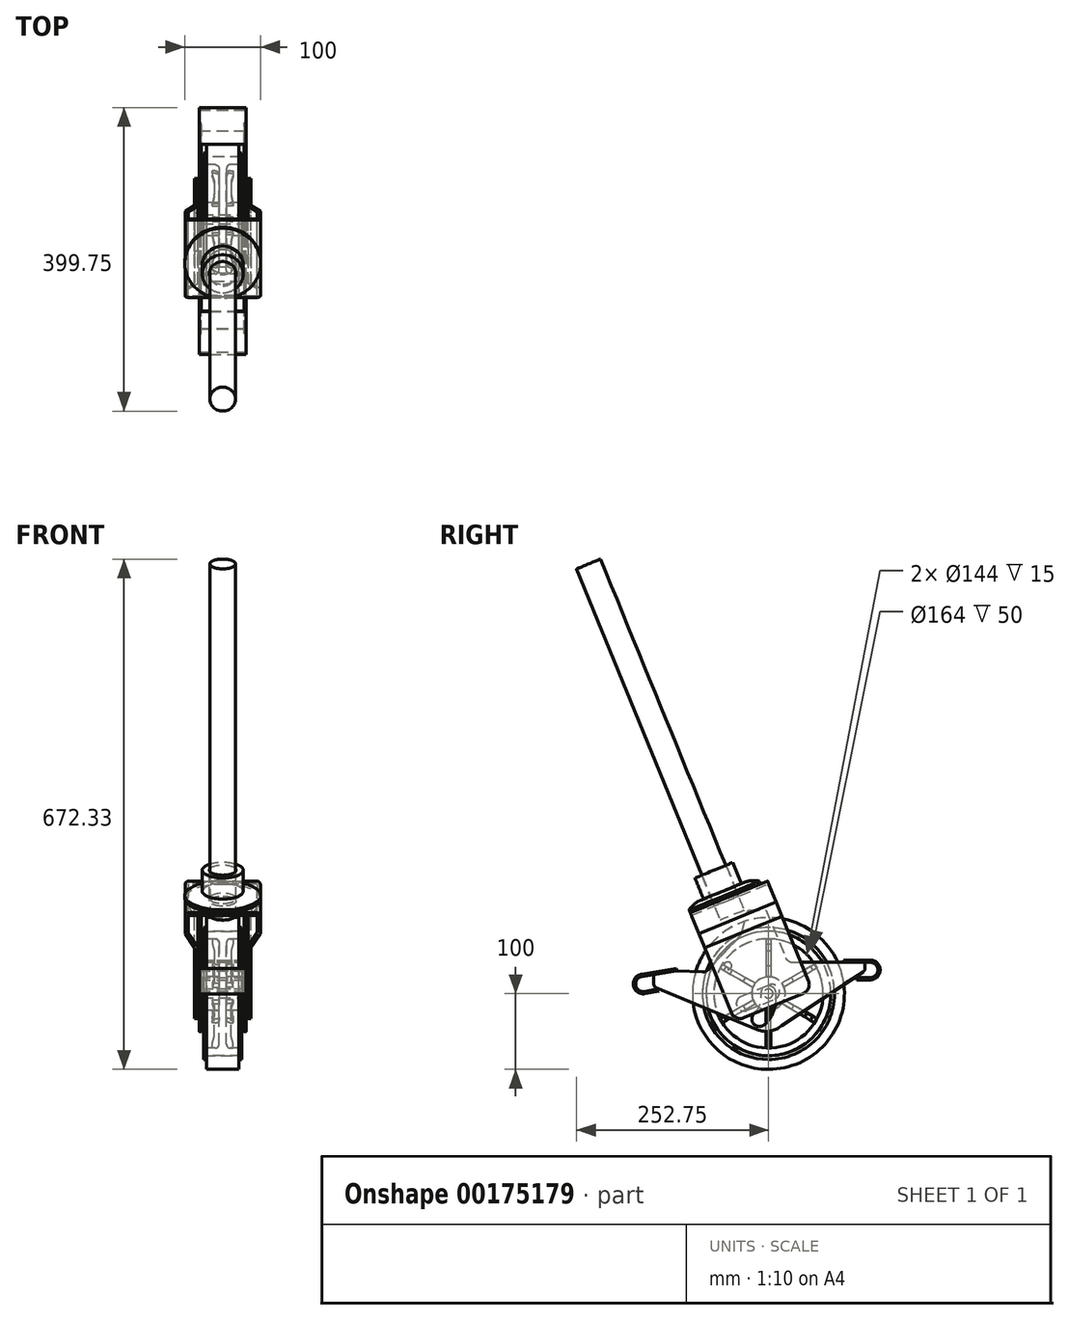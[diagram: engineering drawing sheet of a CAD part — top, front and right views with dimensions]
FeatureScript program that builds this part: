
annotation { "Feature Type Name" : "Feature", "Feature Type Description" : "" }
export const myFeature = defineFeature(function(context is Context, id is Id, definition is map)
    precondition{}
    {
        {
            var Q0;
            Q0=qCreatedBy(makeId("Front.planeOp"),FACE);
            var sketch = newSketch(context, id + "F0", { "sketchPlane" : qUnion([Q0])});
            skLineSegment(sketch, "E0", {"start": v(0, 0) * mm, "end": v(0, 82) * mm});
            skLineSegment(sketch, "E1", {"start": v(0, 82) * mm, "end": v(25, 82) * mm});
            skLineSegment(sketch, "E2", {"start": v(25, 82) * mm, "end": v(25, 72) * mm});
            skLineSegment(sketch, "E3", {"start": v(25, 72) * mm, "end": v(5, 72) * mm});
            skLineSegment(sketch, "E4", {"start": v(5, 72) * mm, "end": v(5, 22) * mm});
            skLineSegment(sketch, "E5", {"start": v(5, 22) * mm, "end": v(27.5, 22) * mm});
            skLineSegment(sketch, "E6", {"start": v(27.5, 22) * mm, "end": v(27.5, 0) * mm});
            skLineSegment(sketch, "E7", {"start": v(27.5, 0) * mm, "end": v(0, 0) * mm});
            skLineSegment(sketch, "E8.MirrorCS", {"start": v(-27.5, 22) * mm, "end": v(-27.5, 0) * mm});
            skLineSegment(sketch, "E9.MirrorCS", {"start": v(0, 82) * mm, "end": v(-25, 82) * mm});
            skLineSegment(sketch, "E10.MirrorCS", {"start": v(-5, 22) * mm, "end": v(-27.5, 22) * mm});
            skLineSegment(sketch, "E11.MirrorCS", {"start": v(-25, 72) * mm, "end": v(-5, 72) * mm});
            skLineSegment(sketch, "E12.MirrorCS", {"start": v(-27.5, 0) * mm, "end": v(0, 0) * mm});
            skLineSegment(sketch, "E13.MirrorCS", {"start": v(-5, 72) * mm, "end": v(-5, 22) * mm});
            skLineSegment(sketch, "E14.MirrorCS", {"start": v(-25, 82) * mm, "end": v(-25, 72) * mm});
            skSolve(sketch);
        }
        {
            var Q0;
            Q0=makeQuery(id+"F0.imprint","IMPRINT",FACE,{"disambiguationData":[TD([[makeQuery(id+"F0.imprint","IMPRINT",EDGE,{"derivedFrom":sQuery(id+"F0.wireOp",EDGE,"E0")}),-1.0]])]});
            var Q1;
            Q1=makeQuery(id+"F0.imprint","IMPRINT",FACE,{"disambiguationData":[TD([[makeQuery(id+"F0.imprint","IMPRINT",EDGE,{"derivedFrom":sQuery(id+"F0.wireOp",EDGE,"E0")}),1.0]])]});
            var Q2;
            Q2=sQuery(id+"F0.wireOp",EDGE,"E12.MirrorCS");
            revolve(context, id + "F1", {"entities" : qUnion([Q0, Q1]), "axis" : qUnion([Q2]), "revolveType" : RevolveType.FULL});
        }
        {
            var Q0;
            Q0=qCreatedBy(makeId("Front.planeOp"),FACE);
            var sketch = newSketch(context, id + "F2", { "sketchPlane" : qUnion([Q0])});
            skLineSegment(sketch, "E15.0.0", {"start": v(5, 67) * mm, "end": v(5, 22) * mm});
            skLineSegment(sketch, "E16", {"start": v(13.5, 22) * mm, "end": v(5, 22) * mm});
            skLineSegment(sketch, "E17", {"start": v(10, 72) * mm, "end": v(13.5, 72) * mm});
            skLineSegment(sketch, "E18", {"start": v(13.5, 72) * mm, "end": v(13.5, 65.54) * mm});
            skLineSegment(sketch, "E19", {"start": v(13.5, 65.54) * mm, "end": v(11, 56.5) * mm});
            skLineSegment(sketch, "E20", {"start": v(11, 56.5) * mm, "end": v(11, 36.5) * mm});
            skLineSegment(sketch, "E21", {"start": v(11, 36.5) * mm, "end": v(13.5, 22) * mm});
            skPoint(sketch, "E22.orphan", {"position": v(5, -72) * mm});
            skPoint(sketch, "E23.visualSharp", {"position": v(5, 72) * mm});
            skArc(sketch, "E23.filletArc", {"start": v(10, 72) * mm, "mid": v(6.46, 70.54) * mm, "end": v(5, 67) * mm});
            skSolve(sketch);
        }
        {
            var Q0;
            Q0=makeQuery(id+"F2.imprint","IMPRINT",FACE,{"disambiguationData":[TD([[makeQuery(id+"F2.imprint","IMPRINT",EDGE,{"derivedFrom":sQuery(id+"F2.wireOp",EDGE,"E15.0.0")}),1.0]])]});
            extrude(context, id + "F3", {"entities" : qUnion([Q0]), "endBound" : BoundingType.SYMMETRIC, "depth" : 6 * mm});
        }
        {
            var Q0;
            Q0=makeQuery(id+"F1.opRevolve","SWEPT_EDGE",EDGE,{"disambiguationData":[OSD([sQuery(id+"F0.wireOp",EDGE,"E3"),sQuery(id+"F0.wireOp",EDGE,"E4")])]});
            var Q1;
            Q1=makeQuery(id+"F1.opRevolve","SWEPT_EDGE",EDGE,{"disambiguationData":[OSD([sQuery(id+"F0.wireOp",EDGE,"E11.MirrorCS"),sQuery(id+"F0.wireOp",EDGE,"E13.MirrorCS")])]});
            fillet(context, id + "F4", {"entities" : qUnion([Q0, Q1]), "radius" : 5 * mm, "tangentPropagation" : true, "allowEdgeOverflow" : false});
        }
        {
            var Q0;
            Q0=makeQuery(id+"F1.opRevolve","SWEPT_FACE",FACE,{"disambiguationData":[OSD([sQuery(id+"F0.wireOp",EDGE,"E6")])]});
            var sketch = newSketch(context, id + "F5", { "sketchPlane" : qUnion([Q0])});
            skCircle(sketch, "E24", {"center": v(0, 0) * mm, "radius": 6 * mm});
            skSolve(sketch);
        }
        {
            var Q0;
            Q0 = qSketchRegion(id + "F5", true);
            extrude(context, id + "F6", {"entities" : qUnion([Q0]), "operationType" : NewBodyOperationType.REMOVE, "endBound" : BoundingType.UP_TO_NEXT, "oppositeDirection" : true, "depth" : 25 * mm});
        }
        {
            var Q0;
            Q0=makeQuery(id+"F3.opExtrude","SWEPT_BODY",BODY,{"disambiguationData":[OSD([sQuery(id+"F2.wireOp",EDGE,"E15.0.0"),sQuery(id+"F2.wireOp",EDGE,"E16"),sQuery(id+"F2.wireOp",EDGE,"E17"),sQuery(id+"F2.wireOp",EDGE,"E18"),sQuery(id+"F2.wireOp",EDGE,"E19"),sQuery(id+"F2.wireOp",EDGE,"E20"),sQuery(id+"F2.wireOp",EDGE,"E21"),sQuery(id+"F2.wireOp",EDGE,"E23.filletArc")])]});
            var Q1;
            Q1=makeQuery(id+"F6.boolean.opBoolean","COPY",FACE,{"derivedFrom":makeQuery(id+"F6.opExtrude","SWEPT_FACE",FACE,{"disambiguationData":[OSD([sQuery(id+"F5.wireOp",EDGE,"E24")])]})});
            circularPattern(context, id + "F7", {"entities" : qUnion([Q0]), "axis" : qUnion([Q1]), "angle" : 360 * degree, "instanceCount" : 6, "equalSpace" : true});
        }
        {
            var Q0;
            Q0=makeQuery(id+"F3.opExtrude","SWEPT_BODY",BODY,{"disambiguationData":[OSD([sQuery(id+"F2.wireOp",EDGE,"E15.0.0"),sQuery(id+"F2.wireOp",EDGE,"E16"),sQuery(id+"F2.wireOp",EDGE,"E17"),sQuery(id+"F2.wireOp",EDGE,"E18"),sQuery(id+"F2.wireOp",EDGE,"E19"),sQuery(id+"F2.wireOp",EDGE,"E20"),sQuery(id+"F2.wireOp",EDGE,"E21"),sQuery(id+"F2.wireOp",EDGE,"E23.filletArc")])]});
            var Q1;
            Q1=makeQuery(id+"F7.opPattern","COPY",BODY,{"derivedFrom":makeQuery(id+"F3.opExtrude","SWEPT_BODY",BODY,{"disambiguationData":[OSD([sQuery(id+"F2.wireOp",EDGE,"E15.0.0"),sQuery(id+"F2.wireOp",EDGE,"E16"),sQuery(id+"F2.wireOp",EDGE,"E17"),sQuery(id+"F2.wireOp",EDGE,"E18"),sQuery(id+"F2.wireOp",EDGE,"E19"),sQuery(id+"F2.wireOp",EDGE,"E20"),sQuery(id+"F2.wireOp",EDGE,"E21"),sQuery(id+"F2.wireOp",EDGE,"E23.filletArc")])]}),"instanceName":"5"});
            var Q2;
            Q2=makeQuery(id+"F7.opPattern","COPY",BODY,{"derivedFrom":makeQuery(id+"F3.opExtrude","SWEPT_BODY",BODY,{"disambiguationData":[OSD([sQuery(id+"F2.wireOp",EDGE,"E15.0.0"),sQuery(id+"F2.wireOp",EDGE,"E16"),sQuery(id+"F2.wireOp",EDGE,"E17"),sQuery(id+"F2.wireOp",EDGE,"E18"),sQuery(id+"F2.wireOp",EDGE,"E19"),sQuery(id+"F2.wireOp",EDGE,"E20"),sQuery(id+"F2.wireOp",EDGE,"E21"),sQuery(id+"F2.wireOp",EDGE,"E23.filletArc")])]}),"instanceName":"4"});
            var Q3;
            Q3=makeQuery(id+"F7.opPattern","COPY",BODY,{"derivedFrom":makeQuery(id+"F3.opExtrude","SWEPT_BODY",BODY,{"disambiguationData":[OSD([sQuery(id+"F2.wireOp",EDGE,"E15.0.0"),sQuery(id+"F2.wireOp",EDGE,"E16"),sQuery(id+"F2.wireOp",EDGE,"E17"),sQuery(id+"F2.wireOp",EDGE,"E18"),sQuery(id+"F2.wireOp",EDGE,"E19"),sQuery(id+"F2.wireOp",EDGE,"E20"),sQuery(id+"F2.wireOp",EDGE,"E21"),sQuery(id+"F2.wireOp",EDGE,"E23.filletArc")])]}),"instanceName":"3"});
            var Q4;
            Q4=makeQuery(id+"F7.opPattern","COPY",BODY,{"derivedFrom":makeQuery(id+"F3.opExtrude","SWEPT_BODY",BODY,{"disambiguationData":[OSD([sQuery(id+"F2.wireOp",EDGE,"E15.0.0"),sQuery(id+"F2.wireOp",EDGE,"E16"),sQuery(id+"F2.wireOp",EDGE,"E17"),sQuery(id+"F2.wireOp",EDGE,"E18"),sQuery(id+"F2.wireOp",EDGE,"E19"),sQuery(id+"F2.wireOp",EDGE,"E20"),sQuery(id+"F2.wireOp",EDGE,"E21"),sQuery(id+"F2.wireOp",EDGE,"E23.filletArc")])]}),"instanceName":"2"});
            var Q5;
            Q5=makeQuery(id+"F7.opPattern","COPY",BODY,{"derivedFrom":makeQuery(id+"F3.opExtrude","SWEPT_BODY",BODY,{"disambiguationData":[OSD([sQuery(id+"F2.wireOp",EDGE,"E15.0.0"),sQuery(id+"F2.wireOp",EDGE,"E16"),sQuery(id+"F2.wireOp",EDGE,"E17"),sQuery(id+"F2.wireOp",EDGE,"E18"),sQuery(id+"F2.wireOp",EDGE,"E19"),sQuery(id+"F2.wireOp",EDGE,"E20"),sQuery(id+"F2.wireOp",EDGE,"E21"),sQuery(id+"F2.wireOp",EDGE,"E23.filletArc")])]}),"instanceName":"1"});
            var Q6;
            Q6=qCreatedBy(makeId("Right.planeOp"),FACE);
            mirror(context, id + "F8", {"entities" : qUnion([Q0, Q1, Q2, Q3, Q4, Q5]), "mirrorPlane" : qUnion([Q6])});
        }
        {
            var Q0;
            Q0=qCreatedBy(makeId("Top.planeOp"),FACE);
            var sketch = newSketch(context, id + "F9", { "sketchPlane" : qUnion([Q0])});
            skLineSegment(sketch, "E25", {"start": v(-890.97, -1000.33) * mm, "end": v(-890.97, -1003.33) * mm});
            skLineSegment(sketch, "E26", {"start": v(-890.97, -1003.33) * mm, "end": v(-894.06, -1003.33) * mm});
            skLineSegment(sketch, "E27", {"start": v(-1283.73, -1003.33) * mm, "end": v(-1283.73, -1396.22) * mm});
            skLineSegment(sketch, "E28", {"start": v(-1283.73, -1396.22) * mm, "end": v(-1690.1, -1396.22) * mm});
            skLineSegment(sketch, "E29", {"start": v(-1690.1, -1396.22) * mm, "end": v(-1690.1, -1802.4) * mm});
            skLineSegment(sketch, "E30", {"start": v(-1690.1, -1802.4) * mm, "end": v(-2098.59, -1802.4) * mm});
            skLineSegment(sketch, "E31", {"start": v(-2098.59, -1802.4) * mm, "end": v(-2098.59, -2210.69) * mm});
            skLineSegment(sketch, "E32", {"start": v(-890.97, -1000.33) * mm, "end": v(-910.8, -1000.33) * mm});
            skLineSegment(sketch, "E33", {"start": v(-910.8, -1000.33) * mm, "end": v(-910.8, -1003.33) * mm});
            skLineSegment(sketch, "E34", {"start": v(-894.06, -1003.33) * mm, "end": v(-894.06, -1005.54) * mm});
            skLineSegment(sketch, "E35", {"start": v(-894.06, -1005.54) * mm, "end": v(-907.53, -1005.54) * mm});
            skLineSegment(sketch, "E36", {"start": v(-907.53, -1005.54) * mm, "end": v(-907.53, -1003.33) * mm});
            skLineSegment(sketch, "E37.trimOffspring", {"start": v(-907.53, -1003.33) * mm, "end": v(-910.8, -1003.33) * mm});
            skLineSegment(sketch, "E38", {"start": v(25, -87) * mm, "end": v(21.48, -87) * mm});
            skLineSegment(sketch, "E39", {"start": v(21.48, -87) * mm, "end": v(21.48, -100) * mm});
            skLineSegment(sketch, "E40", {"start": v(21.48, -100) * mm, "end": v(-21.52, -100) * mm});
            skLineSegment(sketch, "E41", {"start": v(-21.52, -100) * mm, "end": v(-21.52, -87) * mm});
            skLineSegment(sketch, "E42", {"start": v(-21.52, -87) * mm, "end": v(-25.02, -87) * mm});
            skLineSegment(sketch, "E43.0", {"start": v(25, -87) * mm, "end": v(25, -82) * mm});
            skLineSegment(sketch, "E43.1", {"start": v(-25, -87) * mm, "end": v(-25, -82) * mm});
            skLineSegment(sketch, "E44", {"start": v(-25, -82) * mm, "end": v(25, -82) * mm});
            skPoint(sketch, "E45.orphan", {"position": v(25, 82) * mm});
            skPoint(sketch, "E46.orphan", {"position": v(-25, 82) * mm});
            skSolve(sketch);
        }
        {
            var Q0;
            {var subQ3=sQuery(id+"F9.wireOp",EDGE,"E39");Q0=makeQuery(id+"F9.imprint","IMPRINT",FACE,{"disambiguationData":[TD([[makeQuery(id+"F9.imprint","IMPRINT",EDGE,{"derivedFrom":subQ3}),-1.0]])]});}
            var Q1;
            Q1=makeQuery(id+"F1.opRevolve","SWEPT_FACE",FACE,{"disambiguationData":[OSD([sQuery(id+"F0.wireOp",EDGE,"E5")])]});
            revolve(context, id + "F10", {"entities" : qUnion([Q0]), "axis" : qUnion([Q1]), "revolveType" : RevolveType.FULL});
        }
        {
            var Q0;
            Q0=qCreatedBy(makeId("Right.planeOp"),FACE);
            cPlane(context, id + "F11", {"entities" : qUnion([Q0]), "cplaneType" : CPlaneType.OFFSET, "offset" : 28 * mm, "width" : 150 * mm, "height" : 150 * mm});
        }
        {
            var Q0;
            Q0=qCreatedBy(id+"F11.planeOp",FACE);
            var sketch = newSketch(context, id + "F12", { "sketchPlane" : qUnion([Q0])});
            skArc(sketch, "E47", {"start": v(9.92, 1.23) * mm, "mid": v(-1.23, 9.92) * mm, "end": v(-9.92, -1.23) * mm});
            skLineSegment(sketch, "E48", {"start": v(31.86, 41) * mm, "end": v(127, 41) * mm});
            skLineSegment(sketch, "E49", {"start": v(127, 41) * mm, "end": v(127, 32.7) * mm});
            skArc(sketch, "E50", {"start": v(-14.51, -47.7) * mm, "mid": v(1.93, -49.6) * mm, "end": v(16.88, -42.47) * mm});
            skLineSegment(sketch, "E51", {"start": v(124.75, 28.52) * mm, "end": v(16.88, -42.47) * mm});
            skLineSegment(sketch, "E52", {"start": v(-150.97, 25) * mm, "end": v(-150.97, 12.34) * mm});
            skLineSegment(sketch, "E53", {"start": v(-147.89, 7.72) * mm, "end": v(-14.51, -47.7) * mm});
            skLineSegment(sketch, "E54", {"start": v(-150.97, 25) * mm, "end": v(-120.97, 30) * mm});
            skLineSegment(sketch, "E55", {"start": v(-120.97, 30) * mm, "end": v(-87.39, 28.24) * mm});
            skLineSegment(sketch, "E56", {"start": v(-79.6, 31.36) * mm, "end": v(-37.27, 76.13) * mm});
            skLineSegment(sketch, "E57", {"start": v(-34.88, 80.41) * mm, "end": v(-27, 109.83) * mm});
            skLineSegment(sketch, "E58", {"start": v(-27, 109.83) * mm, "end": v(-3, 109.83) * mm});
            skLineSegment(sketch, "E59", {"start": v(-3, 109.83) * mm, "end": v(22.6, 47.22) * mm});
            skPoint(sketch, "E60.visualSharp", {"position": v(-150.97, 9) * mm});
            skArc(sketch, "E60.filletArc", {"start": v(-150.97, 12.34) * mm, "mid": v(-150.13, 9.56) * mm, "end": v(-147.89, 7.72) * mm});
            skPoint(sketch, "E61.visualSharp", {"position": v(127, 30) * mm});
            skArc(sketch, "E61.filletArc", {"start": v(124.75, 28.52) * mm, "mid": v(126.4, 30.32) * mm, "end": v(127, 32.7) * mm});
            skPoint(sketch, "E62.visualSharp", {"position": v(25.14, 41) * mm});
            skArc(sketch, "E62.filletArc", {"start": v(22.6, 47.22) * mm, "mid": v(26.28, 42.7) * mm, "end": v(31.86, 41) * mm});
            skPoint(sketch, "E63.visualSharp", {"position": v(-82.77, 28) * mm});
            skArc(sketch, "E63.filletArc", {"start": v(-87.39, 28.24) * mm, "mid": v(-83.15, 28.94) * mm, "end": v(-79.6, 31.36) * mm});
            skPoint(sketch, "E64.visualSharp", {"position": v(-35.54, 77.97) * mm});
            skArc(sketch, "E64.filletArc", {"start": v(-37.27, 76.13) * mm, "mid": v(-35.81, 78.13) * mm, "end": v(-34.88, 80.41) * mm});
            skArc(sketch, "E65", {"start": v(-18.77, -26.43) * mm, "mid": v(-18.97, -40.57) * mm, "end": v(-4.83, -40.77) * mm});
            skArc(sketch, "E66", {"start": v(-4.83, -40.77) * mm, "mid": v(7.48, -21.5) * mm, "end": v(9.92, 1.23) * mm});
            skArc(sketch, "E67.0", {"start": v(-18.77, -26.43) * mm, "mid": v(-11.39, -14.87) * mm, "end": v(-9.92, -1.23) * mm});
            skCircle(sketch, "E68", {"center": v(-53.5, 36.5) * mm, "radius": 5 * mm});
            skSolve(sketch);
        }
        {
            var Q0;
            Q0 = qSketchRegion(id + "F12", true);
            extrude(context, id + "F13", {"entities" : qUnion([Q0]), "depth" : 3 * mm});
        }
        {
            var Q0;
            Q0=makeQuery(id+"F13.opExtrude","SWEPT_BODY",BODY,{"disambiguationData":[OSD([sQuery(id+"F12.wireOp",EDGE,"E47"),sQuery(id+"F12.wireOp",EDGE,"E48"),sQuery(id+"F12.wireOp",EDGE,"E49"),sQuery(id+"F12.wireOp",EDGE,"E50"),sQuery(id+"F12.wireOp",EDGE,"E51"),sQuery(id+"F12.wireOp",EDGE,"E52"),sQuery(id+"F12.wireOp",EDGE,"E53"),sQuery(id+"F12.wireOp",EDGE,"E54"),sQuery(id+"F12.wireOp",EDGE,"E55"),sQuery(id+"F12.wireOp",EDGE,"E56"),sQuery(id+"F12.wireOp",EDGE,"E57"),sQuery(id+"F12.wireOp",EDGE,"E58"),sQuery(id+"F12.wireOp",EDGE,"E59"),sQuery(id+"F12.wireOp",EDGE,"E60.filletArc"),sQuery(id+"F12.wireOp",EDGE,"E61.filletArc"),sQuery(id+"F12.wireOp",EDGE,"E62.filletArc"),sQuery(id+"F12.wireOp",EDGE,"E63.filletArc"),sQuery(id+"F12.wireOp",EDGE,"E64.filletArc"),sQuery(id+"F12.wireOp",EDGE,"E65"),sQuery(id+"F12.wireOp",EDGE,"E66"),sQuery(id+"F12.wireOp",EDGE,"E67.0"),sQuery(id+"F12.wireOp",EDGE,"E68")])]});
            var Q1;
            Q1=qCreatedBy(makeId("Right.planeOp"),FACE);
            mirror(context, id + "F14", {"entities" : qUnion([Q0]), "mirrorPlane" : qUnion([Q1])});
        }
        {
            var Q0;
            Q0=makeQuery(id+"F13.opExtrude","CAP_FACE",FACE,{"disambiguationData":[OSD([sQuery(id+"F12.wireOp",EDGE,"E47"),sQuery(id+"F12.wireOp",EDGE,"E48"),sQuery(id+"F12.wireOp",EDGE,"E49"),sQuery(id+"F12.wireOp",EDGE,"E50"),sQuery(id+"F12.wireOp",EDGE,"E51"),sQuery(id+"F12.wireOp",EDGE,"E52"),sQuery(id+"F12.wireOp",EDGE,"E53"),sQuery(id+"F12.wireOp",EDGE,"E54"),sQuery(id+"F12.wireOp",EDGE,"E55"),sQuery(id+"F12.wireOp",EDGE,"E56"),sQuery(id+"F12.wireOp",EDGE,"E57"),sQuery(id+"F12.wireOp",EDGE,"E58"),sQuery(id+"F12.wireOp",EDGE,"E59"),sQuery(id+"F12.wireOp",EDGE,"E60.filletArc"),sQuery(id+"F12.wireOp",EDGE,"E61.filletArc"),sQuery(id+"F12.wireOp",EDGE,"E62.filletArc"),sQuery(id+"F12.wireOp",EDGE,"E63.filletArc"),sQuery(id+"F12.wireOp",EDGE,"E64.filletArc"),sQuery(id+"F12.wireOp",EDGE,"E65"),sQuery(id+"F12.wireOp",EDGE,"E66"),sQuery(id+"F12.wireOp",EDGE,"E67.0"),sQuery(id+"F12.wireOp",EDGE,"E68")])],"isStart":false});
            var sketch = newSketch(context, id + "F15", { "sketchPlane" : qUnion([Q0])});
            skLineSegment(sketch, "E69.1", {"start": v(-166.61, 22.4) * mm, "end": v(-120.97, 30) * mm});
            skArc(sketch, "E70", {"start": v(-166.61, 22.4) * mm, "mid": v(-174.8, 10.74) * mm, "end": v(-163.03, 2.72) * mm});
            skPoint(sketch, "E71.orphan", {"position": v(-150.97, 25) * mm});
            skLineSegment(sketch, "E72", {"start": v(-163.03, 2.72) * mm, "end": v(-144.61, 6.36) * mm});
            skLineSegment(sketch, "E73.0", {"start": v(-167.1, 25.35) * mm, "end": v(-121.46, 32.96) * mm});
            skArc(sketch, "E73.1", {"start": v(-167.1, 25.35) * mm, "mid": v(-177.76, 10.2) * mm, "end": v(-162.45, -0.22) * mm});
            skLineSegment(sketch, "E73.2", {"start": v(-162.45, -0.22) * mm, "end": v(-144.03, 3.42) * mm});
            skLineSegment(sketch, "E74", {"start": v(-120.97, 30) * mm, "end": v(-121.46, 32.96) * mm});
            skLineSegment(sketch, "E75", {"start": v(-144.03, 3.42) * mm, "end": v(-144.61, 6.36) * mm});
            skSolve(sketch);
        }
        {
            var Q0;
            Q0 = qSketchRegion(id + "F15", true);
            var Q1;
            Q1=makeQuery(id+"F14.opPattern","COPY",FACE,{"derivedFrom":makeQuery(id+"F13.opExtrude","CAP_FACE",FACE,{"disambiguationData":[OSD([sQuery(id+"F12.wireOp",EDGE,"E47"),sQuery(id+"F12.wireOp",EDGE,"E48"),sQuery(id+"F12.wireOp",EDGE,"E49"),sQuery(id+"F12.wireOp",EDGE,"E50"),sQuery(id+"F12.wireOp",EDGE,"E51"),sQuery(id+"F12.wireOp",EDGE,"E52"),sQuery(id+"F12.wireOp",EDGE,"E53"),sQuery(id+"F12.wireOp",EDGE,"E54"),sQuery(id+"F12.wireOp",EDGE,"E55"),sQuery(id+"F12.wireOp",EDGE,"E56"),sQuery(id+"F12.wireOp",EDGE,"E57"),sQuery(id+"F12.wireOp",EDGE,"E58"),sQuery(id+"F12.wireOp",EDGE,"E59"),sQuery(id+"F12.wireOp",EDGE,"E60.filletArc"),sQuery(id+"F12.wireOp",EDGE,"E61.filletArc"),sQuery(id+"F12.wireOp",EDGE,"E62.filletArc"),sQuery(id+"F12.wireOp",EDGE,"E63.filletArc"),sQuery(id+"F12.wireOp",EDGE,"E64.filletArc"),sQuery(id+"F12.wireOp",EDGE,"E65"),sQuery(id+"F12.wireOp",EDGE,"E66"),sQuery(id+"F12.wireOp",EDGE,"E67.0"),sQuery(id+"F12.wireOp",EDGE,"E68")])],"isStart":false}),"instanceName":"1"});
            extrude(context, id + "F16", {"entities" : qUnion([Q0]), "endBound" : BoundingType.UP_TO_SURFACE, "oppositeDirection" : true, "endBoundEntityFace" : qUnion([Q1]), "depth" : 25 * mm});
        }
        {
            var Q0;
            Q0=makeQuery(id+"F13.opExtrude","CAP_FACE",FACE,{"disambiguationData":[OSD([sQuery(id+"F12.wireOp",EDGE,"E47"),sQuery(id+"F12.wireOp",EDGE,"E48"),sQuery(id+"F12.wireOp",EDGE,"E49"),sQuery(id+"F12.wireOp",EDGE,"E50"),sQuery(id+"F12.wireOp",EDGE,"E51"),sQuery(id+"F12.wireOp",EDGE,"E52"),sQuery(id+"F12.wireOp",EDGE,"E53"),sQuery(id+"F12.wireOp",EDGE,"E54"),sQuery(id+"F12.wireOp",EDGE,"E55"),sQuery(id+"F12.wireOp",EDGE,"E56"),sQuery(id+"F12.wireOp",EDGE,"E57"),sQuery(id+"F12.wireOp",EDGE,"E58"),sQuery(id+"F12.wireOp",EDGE,"E59"),sQuery(id+"F12.wireOp",EDGE,"E60.filletArc"),sQuery(id+"F12.wireOp",EDGE,"E61.filletArc"),sQuery(id+"F12.wireOp",EDGE,"E62.filletArc"),sQuery(id+"F12.wireOp",EDGE,"E63.filletArc"),sQuery(id+"F12.wireOp",EDGE,"E64.filletArc"),sQuery(id+"F12.wireOp",EDGE,"E65"),sQuery(id+"F12.wireOp",EDGE,"E66"),sQuery(id+"F12.wireOp",EDGE,"E67.0"),sQuery(id+"F12.wireOp",EDGE,"E68")])],"isStart":false});
            var sketch = newSketch(context, id + "F17", { "sketchPlane" : qUnion([Q0])});
            skLineSegment(sketch, "E76.0.0", {"start": v(-37.27, 76.13) * mm, "end": v(-79.6, 31.36) * mm});
            skArc(sketch, "E76.0.1", {"start": v(-79.6, 31.36) * mm, "mid": v(-83.15, 28.94) * mm, "end": v(-87.39, 28.24) * mm});
            skLineSegment(sketch, "E76.0.2", {"start": v(-87.39, 28.24) * mm, "end": v(-120.97, 30) * mm});
            skLineSegment(sketch, "E76.0.3", {"start": v(-120.97, 30) * mm, "end": v(-150.97, 25) * mm});
            skLineSegment(sketch, "E76.0.4", {"start": v(-150.97, 25) * mm, "end": v(-150.97, 12.34) * mm});
            skArc(sketch, "E76.0.5", {"start": v(-150.97, 12.34) * mm, "mid": v(-150.13, 9.56) * mm, "end": v(-147.89, 7.72) * mm});
            skLineSegment(sketch, "E76.0.6", {"start": v(-147.89, 7.72) * mm, "end": v(-14.51, -47.7) * mm});
            skArc(sketch, "E76.0.7", {"start": v(-14.51, -47.7) * mm, "mid": v(1.93, -49.6) * mm, "end": v(16.88, -42.47) * mm});
            skLineSegment(sketch, "E76.0.11", {"start": v(127, 41) * mm, "end": v(99, 41) * mm});
            skArc(sketch, "E76.0.12", {"start": v(31.86, 41) * mm, "mid": v(26.28, 42.7) * mm, "end": v(22.6, 47.22) * mm});
            skLineSegment(sketch, "E76.0.13", {"start": v(22.6, 47.22) * mm, "end": v(-3, 109.83) * mm});
            skLineSegment(sketch, "E76.0.14", {"start": v(-3, 109.83) * mm, "end": v(-27, 109.83) * mm});
            skLineSegment(sketch, "E76.0.15", {"start": v(-27, 109.83) * mm, "end": v(-34.88, 80.41) * mm});
            skArc(sketch, "E76.0.16", {"start": v(-34.88, 80.41) * mm, "mid": v(-35.81, 78.13) * mm, "end": v(-37.27, 76.13) * mm});
            skLineSegment(sketch, "E76.1", {"start": v(99, 41) * mm, "end": v(134, 41) * mm});
            skArc(sketch, "E77", {"start": v(133.94, 21) * mm, "mid": v(144, 30.97) * mm, "end": v(134, 41) * mm});
            skLineSegment(sketch, "E78", {"start": v(133.94, 21) * mm, "end": v(116.29, 21) * mm});
            skLineSegment(sketch, "E79.0", {"start": v(133.94, 18) * mm, "end": v(116.29, 18) * mm});
            skArc(sketch, "E80.0", {"start": v(133.92, 18) * mm, "mid": v(147, 30.96) * mm, "end": v(134, 44) * mm});
            skLineSegment(sketch, "E81.0", {"start": v(99, 44) * mm, "end": v(134, 44) * mm});
            skLineSegment(sketch, "E82", {"start": v(99, 41) * mm, "end": v(99, 44) * mm});
            skLineSegment(sketch, "E83", {"start": v(116.29, 21) * mm, "end": v(116.29, 18) * mm});
            skSolve(sketch);
        }
        {
            var Q0;
            Q0 = qSketchRegion(id + "F17", true);
            var Q1;
            Q1=makeQuery(id+"F14.opPattern","COPY",FACE,{"derivedFrom":makeQuery(id+"F13.opExtrude","CAP_FACE",FACE,{"disambiguationData":[OSD([sQuery(id+"F12.wireOp",EDGE,"E47"),sQuery(id+"F12.wireOp",EDGE,"E48"),sQuery(id+"F12.wireOp",EDGE,"E49"),sQuery(id+"F12.wireOp",EDGE,"E50"),sQuery(id+"F12.wireOp",EDGE,"E51"),sQuery(id+"F12.wireOp",EDGE,"E52"),sQuery(id+"F12.wireOp",EDGE,"E53"),sQuery(id+"F12.wireOp",EDGE,"E54"),sQuery(id+"F12.wireOp",EDGE,"E55"),sQuery(id+"F12.wireOp",EDGE,"E56"),sQuery(id+"F12.wireOp",EDGE,"E57"),sQuery(id+"F12.wireOp",EDGE,"E58"),sQuery(id+"F12.wireOp",EDGE,"E59"),sQuery(id+"F12.wireOp",EDGE,"E60.filletArc"),sQuery(id+"F12.wireOp",EDGE,"E61.filletArc"),sQuery(id+"F12.wireOp",EDGE,"E62.filletArc"),sQuery(id+"F12.wireOp",EDGE,"E63.filletArc"),sQuery(id+"F12.wireOp",EDGE,"E64.filletArc"),sQuery(id+"F12.wireOp",EDGE,"E65"),sQuery(id+"F12.wireOp",EDGE,"E66"),sQuery(id+"F12.wireOp",EDGE,"E67.0"),sQuery(id+"F12.wireOp",EDGE,"E68")])],"isStart":false}),"instanceName":"1"});
            extrude(context, id + "F18", {"entities" : qUnion([Q0]), "endBound" : BoundingType.UP_TO_SURFACE, "oppositeDirection" : true, "endBoundEntityFace" : qUnion([Q1]), "depth" : 25 * mm});
        }
        {
            var Q0;
            Q0=makeQuery(id+"F13.opExtrude","SWEPT_FACE",FACE,{"disambiguationData":[OSD([sQuery(id+"F12.wireOp",EDGE,"E59")])]});
            cPlane(context, id + "F19", {"entities" : qUnion([Q0]), "cplaneType" : CPlaneType.OFFSET, "offset" : 38.8 * mm, "oppositeDirection" : true, "width" : 150 * mm, "height" : 150 * mm});
        }
        {
            var Q0;
            Q0=qCreatedBy(id+"F19.planeOp",FACE);
            var sketch = newSketch(context, id + "F20", { "sketchPlane" : qUnion([Q0])});
            skLineSegment(sketch, "E84.top", {"start": v(44.5, 133.5) * mm, "end": v(0, 133.5) * mm});
            skLineSegment(sketch, "E84.left", {"start": v(33, -17.5) * mm, "end": v(33, 88.65) * mm});
            skLineSegment(sketch, "E85", {"start": v(45.5, 132.5) * mm, "end": v(45.5, 108.65) * mm});
            skLineSegment(sketch, "E86", {"start": v(45.5, 108.65) * mm, "end": v(33, 88.65) * mm});
            skLineSegment(sketch, "E87", {"start": v(0, 98.73) * mm, "end": v(0, 133.5) * mm, "construction": true});
            skLineSegment(sketch, "E88.0", {"start": v(44.5, 137.5) * mm, "end": v(0, 137.5) * mm});
            skLineSegment(sketch, "E88.1", {"start": v(49.5, 132.5) * mm, "end": v(49.5, 107.5) * mm});
            skLineSegment(sketch, "E88.2", {"start": v(49.5, 107.5) * mm, "end": v(37, 87.5) * mm});
            skLineSegment(sketch, "E88.3", {"start": v(37, -17.5) * mm, "end": v(37, 87.5) * mm});
            skLineSegment(sketch, "E89", {"start": v(37, -17.5) * mm, "end": v(33, -17.5) * mm});
            skLineSegment(sketch, "E90.MirrorCS", {"start": v(-37, -17.5) * mm, "end": v(-33, -17.5) * mm});
            skLineSegment(sketch, "E91.MirrorCS", {"start": v(-44.5, 137.5) * mm, "end": v(0, 137.5) * mm});
            skLineSegment(sketch, "E92.MirrorCS", {"start": v(-45.5, 108.65) * mm, "end": v(-33, 88.65) * mm});
            skLineSegment(sketch, "E93.MirrorCS", {"start": v(-45.5, 132.5) * mm, "end": v(-45.5, 108.65) * mm});
            skLineSegment(sketch, "E94.MirrorCS", {"start": v(-33, -17.5) * mm, "end": v(-33, 88.65) * mm});
            skLineSegment(sketch, "E95.MirrorCS", {"start": v(-49.5, 132.5) * mm, "end": v(-49.5, 107.5) * mm});
            skLineSegment(sketch, "E96.MirrorCS", {"start": v(-37, -17.5) * mm, "end": v(-37, 87.5) * mm});
            skLineSegment(sketch, "E97.MirrorCS", {"start": v(-44.5, 133.5) * mm, "end": v(0, 133.5) * mm});
            skLineSegment(sketch, "E98.MirrorCS", {"start": v(-49.5, 107.5) * mm, "end": v(-37, 87.5) * mm});
            skPoint(sketch, "E99.visualSharp", {"position": v(45.5, 133.5) * mm});
            skArc(sketch, "E99.filletArc", {"start": v(45.5, 132.5) * mm, "mid": v(45.2, 133.2) * mm, "end": v(44.5, 133.5) * mm});
            skPoint(sketch, "E100.visualSharp", {"position": v(-45.5, 133.5) * mm});
            skArc(sketch, "E100.filletArc", {"start": v(-44.5, 133.5) * mm, "mid": v(-45.2, 133.2) * mm, "end": v(-45.5, 132.5) * mm});
            skPoint(sketch, "E101.visualSharp", {"position": v(-49.5, 137.5) * mm});
            skArc(sketch, "E101.filletArc", {"start": v(-44.5, 137.5) * mm, "mid": v(-48.04, 136.04) * mm, "end": v(-49.5, 132.5) * mm});
            skPoint(sketch, "E102.visualSharp", {"position": v(49.5, 137.5) * mm});
            skArc(sketch, "E102.filletArc", {"start": v(49.5, 132.5) * mm, "mid": v(48.04, 136.04) * mm, "end": v(44.5, 137.5) * mm});
            skSolve(sketch);
        }
        {
            var Q0;
            Q0 = qSketchRegion(id + "F20", true);
            extrude(context, id + "F21", {"entities" : qUnion([Q0]), "endBound" : BoundingType.SYMMETRIC, "oppositeDirection" : true, "depth" : 110 * mm});
        }
        {
            var Q0;
            Q0=makeQuery(id+"F21.opExtrude","CAP_EDGE",EDGE,{"disambiguationData":[OSD([sQuery(id+"F20.wireOp",EDGE,"E90.MirrorCS")])],"isStart":true});
            var Q1;
            Q1=makeQuery(id+"F21.opExtrude","CAP_EDGE",EDGE,{"disambiguationData":[OSD([sQuery(id+"F20.wireOp",EDGE,"E90.MirrorCS")])],"isStart":false});
            var Q2;
            Q2=makeQuery(id+"F21.opExtrude","CAP_EDGE",EDGE,{"disambiguationData":[OSD([sQuery(id+"F20.wireOp",EDGE,"E89")])],"isStart":false});
            var Q3;
            Q3=makeQuery(id+"F21.opExtrude","CAP_EDGE",EDGE,{"disambiguationData":[OSD([sQuery(id+"F20.wireOp",EDGE,"E89")])],"isStart":true});
            fillet(context, id + "F22", {"entities" : qUnion([Q0, Q1, Q2, Q3]), "radius" : 13 * mm, "tangentPropagation" : true, "allowEdgeOverflow" : false});
        }
        {
            var Q0;
            Q0=makeQuery(id+"F21.opExtrude","SWEPT_FACE",FACE,{"disambiguationData":[OSD([sQuery(id+"F20.wireOp",EDGE,"E88.3")])]});
            var sketch = newSketch(context, id + "F23", { "sketchPlane" : qUnion([Q0])});
            skLineSegment(sketch, "E103", {"start": v(36.85, -15.07) * mm, "end": v(-17.88, 7.3) * mm, "construction": true});
            skArc(sketch, "E104", {"start": v(-0.8, 11.13) * mm, "mid": v(-13.92, 5.59) * mm, "end": v(-8.18, -7.45) * mm});
            skArc(sketch, "E105", {"start": v(28.61, -22.5) * mm, "mid": v(41.65, -17.03) * mm, "end": v(36.18, -4) * mm});
            skLineSegment(sketch, "E106", {"start": v(-8.18, -7.45) * mm, "end": v(28.61, -22.5) * mm});
            skLineSegment(sketch, "E107", {"start": v(-0.9, 11.17) * mm, "end": v(36.18, -4) * mm});
            skSolve(sketch);
        }
        {
            var Q0;
            Q0 = qSketchRegion(id + "F23", true);
            extrude(context, id + "F24", {"entities" : qUnion([Q0]), "operationType" : NewBodyOperationType.REMOVE, "endBound" : BoundingType.UP_TO_NEXT, "oppositeDirection" : true, "depth" : 25 * mm});
        }
        {
            var Q0;
            Q0=makeQuery(id+"F1.opRevolve","SWEPT_FACE",FACE,{"disambiguationData":[OSD([sQuery(id+"F0.wireOp",EDGE,"E14.MirrorCS")])]});
            cPlane(context, id + "F25", {"entities" : qUnion([Q0]), "cplaneType" : CPlaneType.OFFSET, "offset" : 25 * mm, "oppositeDirection" : true, "width" : 150 * mm, "height" : 150 * mm});
        }
        {
            var Q0;
            Q0=makeQuery(id+"F21.opExtrude","SWEPT_FACE",FACE,{"disambiguationData":[OSD([sQuery(id+"F20.wireOp",EDGE,"E88.0"),sQuery(id+"F20.wireOp",EDGE,"E91.MirrorCS")])]});
            var sketch = newSketch(context, id + "F26", { "sketchPlane" : qUnion([Q0])});
            skCircle(sketch, "E108", {"center": v(0, -5) * mm, "radius": 17.5 * mm});
            skPoint(sketch, "E108.centerSnap0", {"position": v(0, -55) * mm});
            skSolve(sketch);
        }
        {
            var Q0;
            Q0 = qSketchRegion(id + "F26", true);
            extrude(context, id + "F27", {"entities" : qUnion([Q0]), "operationType" : NewBodyOperationType.REMOVE, "endBound" : BoundingType.UP_TO_NEXT, "oppositeDirection" : true, "depth" : 25 * mm});
        }
        {
            var Q0;
            Q0=qCreatedBy(id+"F25.planeOp",FACE);
            var sketch = newSketch(context, id + "F28", { "sketchPlane" : qUnion([Q0])});
            skLineSegment(sketch, "E109", {"start": v(56.68, 125.38) * mm, "end": v(60.46, 134.63) * mm});
            skLineSegment(sketch, "E110", {"start": v(102.96, 106.45) * mm, "end": v(104.47, 110.15) * mm});
            skLineSegment(sketch, "E111", {"start": v(89.08, 122.93) * mm, "end": v(60.46, 134.63) * mm});
            skArc(sketch, "E112", {"start": v(89.08, 122.93) * mm, "mid": v(97.76, 117.72) * mm, "end": v(104.47, 110.15) * mm});
            skLineSegment(sketch, "E113.0", {"start": v(102.96, 106.45) * mm, "end": v(56.68, 125.38) * mm});
            skPoint(sketch, "E114.orphan", {"position": v(1.14, 148.08) * mm});
            skSolve(sketch);
        }
        {
            var Q0;
            Q0 = qSketchRegion(id + "F28", true);
            var Q1;
            Q1=sQuery(id+"F28.wireOp",EDGE,"E109");
            revolve(context, id + "F29", {"entities" : qUnion([Q0]), "axis" : qUnion([Q1]), "revolveType" : RevolveType.FULL});
        }
        {
            var Q0;
            Q0=makeQuery(id+"F29.opRevolve","SWEPT_FACE",FACE,{"disambiguationData":[OSD([sQuery(id+"F28.wireOp",EDGE,"E111")])]});
            var sketch = newSketch(context, id + "F30", { "sketchPlane" : qUnion([Q0])});
            skCircle(sketch, "E115", {"center": v(0, -5) * mm, "radius": 17.5 * mm});
            skSolve(sketch);
        }
        {
            var Q0;
            Q0 = qSketchRegion(id + "F30", true);
            extrude(context, id + "F31", {"entities" : qUnion([Q0]), "operationType" : NewBodyOperationType.REMOVE, "oppositeDirection" : true, "depth" : 10 * mm});
        }
        {
            var Q0;
            Q0=makeQuery(id+"F29.opRevolve","SWEPT_FACE",FACE,{"disambiguationData":[OSD([sQuery(id+"F28.wireOp",EDGE,"E111")])]});
            var sketch = newSketch(context, id + "F32", { "sketchPlane" : qUnion([Q0])});
            skCircle(sketch, "E116", {"center": v(0, -5) * mm, "radius": 27 * mm});
            skCircle(sketch, "E117.0", {"center": v(0, -5) * mm, "radius": 17.5 * mm});
            skSolve(sketch);
        }
        {
            var Q0;
            Q0 = qSketchRegion(id + "F32", true);
            extrude(context, id + "F33", {"entities" : qUnion([Q0]), "operationType" : NewBodyOperationType.ADD, "depth" : 30 * mm});
        }
        {
            var Q0;
            Q0=makeQuery(id+"F21.opExtrude","SWEPT_FACE",FACE,{"disambiguationData":[OSD([sQuery(id+"F20.wireOp",EDGE,"E84.top"),sQuery(id+"F20.wireOp",EDGE,"E97.MirrorCS")])]});
            cPlane(context, id + "F34", {"entities" : qUnion([Q0]), "cplaneType" : CPlaneType.OFFSET, "offset" : 20 * mm, "width" : 150 * mm, "height" : 150 * mm});
        }
        {
            var Q0;
            Q0=qCreatedBy(id+"F34.planeOp",FACE);
            var sketch = newSketch(context, id + "F35", { "sketchPlane" : qUnion([Q0])});
            skCircle(sketch, "E118", {"center": v(0, 5.2) * mm, "radius": 17 * mm});
            skSolve(sketch);
        }
        {
            var Q0;
            Q0 = qSketchRegion(id + "F35", true);
            extrude(context, id + "F36", {"entities" : qUnion([Q0]), "oppositeDirection" : true, "depth" : 500 * mm});
        }
    });
